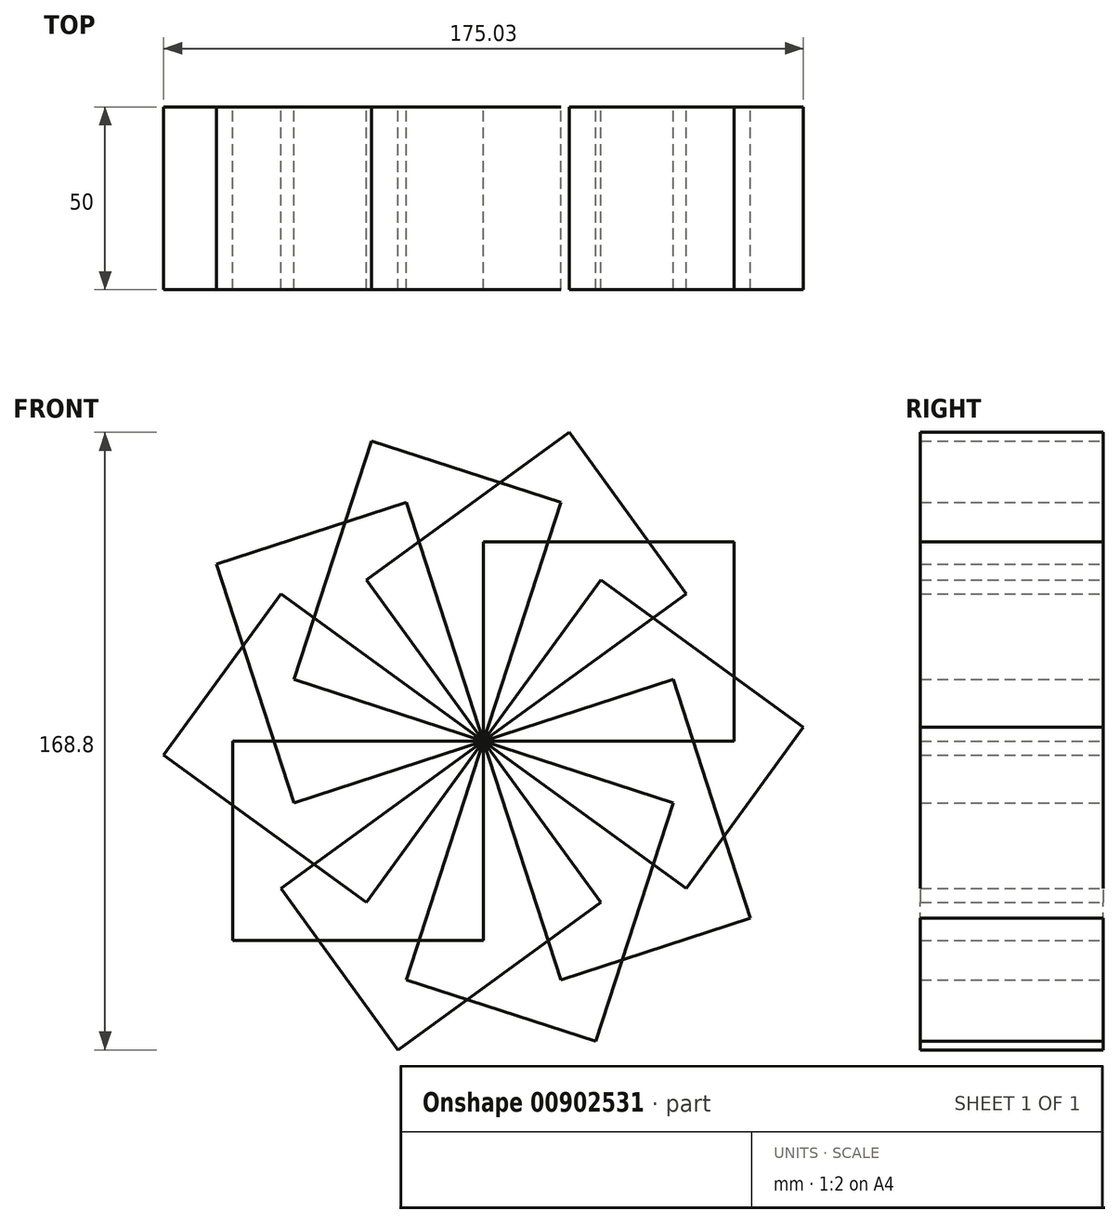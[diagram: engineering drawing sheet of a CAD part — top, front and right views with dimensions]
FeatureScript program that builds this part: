
annotation { "Feature Type Name" : "Feature", "Feature Type Description" : "" }
export const myFeature = defineFeature(function(context is Context, id is Id, definition is map)
    precondition{}
    {
        {
            var Q0;
            Q0=qCreatedBy(makeId("Front.planeOp"),FACE);
            var sketch = newSketch(context, id + "F0", { "sketchPlane" : qUnion([Q0])});
            skLineSegment(sketch, "E0.bottom", {"start": v(-101.86, 20.18) * mm, "end": v(-33.28, 20.18) * mm});
            skLineSegment(sketch, "E0.top", {"start": v(-101.86, -34.32) * mm, "end": v(-33.28, -34.32) * mm});
            skLineSegment(sketch, "E0.left", {"start": v(-101.86, 20.18) * mm, "end": v(-101.86, -34.32) * mm});
            skLineSegment(sketch, "E0.right", {"start": v(-33.28, 20.18) * mm, "end": v(-33.28, -34.32) * mm});
            skSolve(sketch);
        }
        {
            var Q0;
            Q0 = qSketchRegion(id + "F0", true);
            extrude(context, id + "F1", {"entities" : qUnion([Q0]), "depth" : 25 * mm, "offsetDistance" : 25 * mm, "hasSecondDirection" : true, "secondDirectionOppositeDirection" : true, "secondDirectionDepth" : 25 * mm});
        }
        {
            var Q0;
            Q0=makeQuery(id+"F1.opExtrude","SWEPT_BODY",BODY,{"disambiguationData":[OSD([sQuery(id+"F0.wireOp",EDGE,"E0.bottom"),sQuery(id+"F0.wireOp",EDGE,"E0.top"),sQuery(id+"F0.wireOp",EDGE,"E0.left"),sQuery(id+"F0.wireOp",EDGE,"E0.right")])]});
            var Q1;
            Q1=makeQuery(id+"F1.opExtrude","SWEPT_EDGE",EDGE,{"disambiguationData":[OSD([sQuery(id+"F0.wireOp",EDGE,"E0.bottom"),sQuery(id+"F0.wireOp",EDGE,"E0.right")])]});
            circularPattern(context, id + "F2", {"entities" : qUnion([Q0]), "axis" : qUnion([Q1]), "angle" : 360 * degree, "instanceCount" : 10, "equalSpace" : true});
        }
    });
